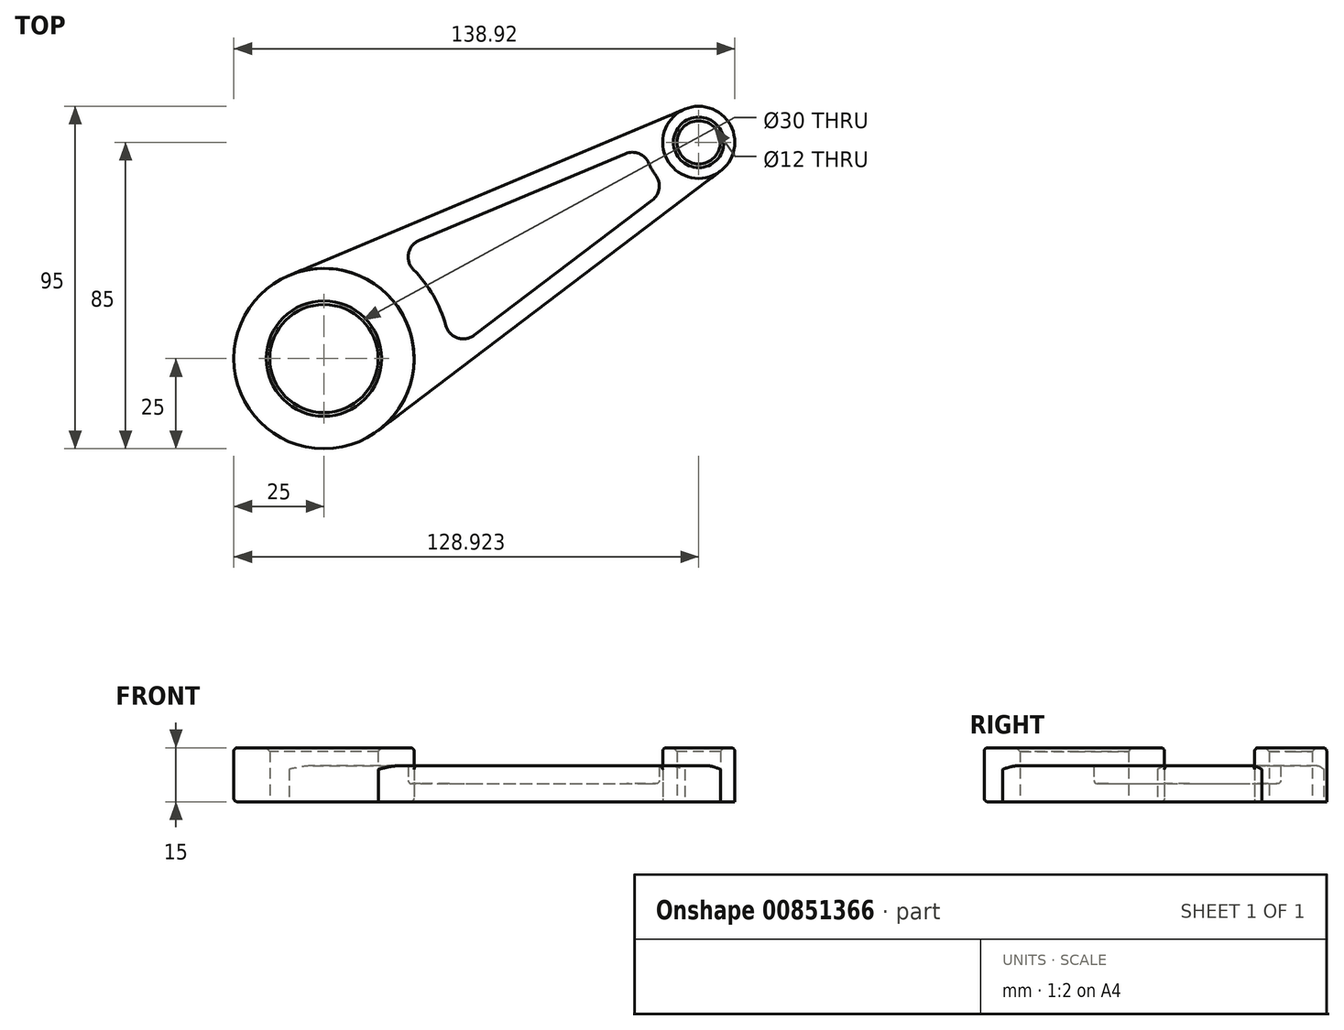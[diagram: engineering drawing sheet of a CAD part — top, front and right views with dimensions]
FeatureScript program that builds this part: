
annotation { "Feature Type Name" : "Feature", "Feature Type Description" : "" }
export const myFeature = defineFeature(function(context is Context, id is Id, definition is map)
    precondition{}
    {
        {
            var Q0;
            Q0=qCreatedBy(makeId("Top.planeOp"),FACE);
            var sketch = newSketch(context, id + "F0", { "sketchPlane" : qUnion([Q0])});
            skLineSegment(sketch, "E0", {"start": v(0, 0) * mm, "end": v(103.92, 60) * mm, "construction": true});
            skLineSegment(sketch, "E1", {"start": v(0, 0) * mm, "end": v(100, 0) * mm, "construction": true});
            skCircle(sketch, "E2", {"center": v(0, 0) * mm, "radius": 25 * mm});
            skCircle(sketch, "E3", {"center": v(103.92, 60) * mm, "radius": 10 * mm});
            skLineSegment(sketch, "E4", {"start": v(-9.7, 23.04) * mm, "end": v(100.04, 69.22) * mm});
            skLineSegment(sketch, "E5", {"start": v(15.1, -19.92) * mm, "end": v(109.97, 52.03) * mm});
            skCircle(sketch, "E6", {"center": v(0, 0) * mm, "radius": 15 * mm});
            skCircle(sketch, "E7", {"center": v(103.92, 60) * mm, "radius": 6 * mm});
            skLineSegment(sketch, "E8.0", {"start": v(34.97, 1.42) * mm, "end": v(95.68, 47.47) * mm});
            skLineSegment(sketch, "E9.0", {"start": v(18.72, 29.57) * mm, "end": v(88.95, 59.12) * mm});
            skArc(sketch, "E10", {"start": v(18.72, 29.57) * mm, "mid": v(30.31, 17.5) * mm, "end": v(34.97, 1.42) * mm});
            skArc(sketch, "E11", {"start": v(88.95, 59.12) * mm, "mid": v(90.93, 52.5) * mm, "end": v(95.68, 47.47) * mm});
            skSolve(sketch);
        }
        {
            var Q0;
            Q0=makeQuery(id+"F0.imprint","IMPRINT",FACE,{"disambiguationData":[TD([[makeQuery(id+"F0.imprint","IMPRINT",EDGE,{"derivedFrom":sQuery(id+"F0.wireOp",EDGE,"E6")}),-1.0]])]});
            var Q1;
            Q1=makeQuery(id+"F0.imprint","IMPRINT",FACE,{"disambiguationData":[TD([[makeQuery(id+"F0.imprint","IMPRINT",EDGE,{"derivedFrom":sQuery(id+"F0.wireOp",EDGE,"E7")}),-1.0]])]});
            extrude(context, id + "F1", {"entities" : qUnion([Q0, Q1]), "depth" : 15 * mm, "offsetDistance" : 25 * mm});
        }
        {
            var Q0;
            {var subQ1=sQuery(id+"F0.wireOp",EDGE,"E4");Q0=makeQuery(id+"F0.imprint","IMPRINT",FACE,{"disambiguationData":[TD([[makeQuery(id+"F0.imprint","IMPRINT",EDGE,{"derivedFrom":subQ1}),-1.0]])]});}
            extrude(context, id + "F2", {"entities" : qUnion([Q0]), "depth" : 10 * mm, "offsetDistance" : 25 * mm});
        }
        {
            var Q0;
            Q0=makeQuery(id+"F0.imprint","IMPRINT",FACE,{"disambiguationData":[TD([[makeQuery(id+"F0.imprint","IMPRINT",EDGE,{"derivedFrom":sQuery(id+"F0.wireOp",EDGE,"E8.0")}),1.0]])]});
            extrude(context, id + "F3", {"entities" : qUnion([Q0]), "operationType" : NewBodyOperationType.ADD, "depth" : 5 * mm, "offsetDistance" : 25 * mm});
        }
        {
            var Q0;
            Q0=makeQuery(id+"F2.opExtrude","CAP_EDGE",EDGE,{"disambiguationData":[OSD([sQuery(id+"F0.wireOp",EDGE,"E2")])],"isStart":false});
            var Q1;
            Q1=makeQuery(id+"F2.opExtrude","CAP_EDGE",EDGE,{"disambiguationData":[OSD([sQuery(id+"F0.wireOp",EDGE,"E3")])],"isStart":false});
            fillet(context, id + "F4", {"entities" : qUnion([Q0, Q1]), "radius" : 1 * mm, "tangentPropagation" : true, "allowEdgeOverflow" : false});
        }
        {
            var Q0;
            Q0=makeQuery(id+"F2.opExtrude","SWEPT_EDGE",EDGE,{"disambiguationData":[OSD([sQuery(id+"F0.wireOp",EDGE,"E9.0"),sQuery(id+"F0.wireOp",EDGE,"E10")])]});
            var Q1;
            Q1=makeQuery(id+"F2.opExtrude","SWEPT_EDGE",EDGE,{"disambiguationData":[OSD([sQuery(id+"F0.wireOp",EDGE,"E8.0"),sQuery(id+"F0.wireOp",EDGE,"E11")])]});
            var Q2;
            Q2=makeQuery(id+"F2.opExtrude","SWEPT_EDGE",EDGE,{"disambiguationData":[OSD([sQuery(id+"F0.wireOp",EDGE,"E9.0"),sQuery(id+"F0.wireOp",EDGE,"E11")])]});
            var Q3;
            Q3=makeQuery(id+"F2.opExtrude","SWEPT_EDGE",EDGE,{"disambiguationData":[OSD([sQuery(id+"F0.wireOp",EDGE,"E8.0"),sQuery(id+"F0.wireOp",EDGE,"E10")])]});
            fillet(context, id + "F5", {"entities" : qUnion([Q0, Q1, Q2, Q3]), "radius" : 5 * mm, "tangentPropagation" : true, "allowEdgeOverflow" : false});
        }
        {
            var Q0;
            Q0=makeQuery(id+"F3.opExtrude","CAP_FACE",FACE,{"disambiguationData":[OSD([sQuery(id+"F0.wireOp",EDGE,"E8.0"),sQuery(id+"F0.wireOp",EDGE,"E9.0"),sQuery(id+"F0.wireOp",EDGE,"E10"),sQuery(id+"F0.wireOp",EDGE,"E11")])],"isStart":false});
            fillet(context, id + "F6", {"entities" : qUnion([Q0]), "radius" : 1 * mm, "tangentPropagation" : true, "allowEdgeOverflow" : false});
        }
        {
            var Q0;
            Q0=makeQuery(id+"F1.opExtrude","CAP_EDGE",EDGE,{"disambiguationData":[OSD([sQuery(id+"F0.wireOp",EDGE,"E3")])],"isStart":false});
            var Q1;
            Q1=makeQuery(id+"F1.opExtrude","CAP_EDGE",EDGE,{"disambiguationData":[OSD([sQuery(id+"F0.wireOp",EDGE,"E2")])],"isStart":false});
            fillet(context, id + "F7", {"entities" : qUnion([Q0, Q1]), "radius" : 1 * mm, "tangentPropagation" : true, "allowEdgeOverflow" : false});
        }
        {
            var Q0;
            Q0=makeQuery(id+"F1.opExtrude","CAP_EDGE",EDGE,{"disambiguationData":[OSD([sQuery(id+"F0.wireOp",EDGE,"E2")])],"isStart":true});
            fillet(context, id + "F8", {"entities" : qUnion([Q0]), "radius" : 1 * mm, "tangentPropagation" : true, "allowEdgeOverflow" : false});
        }
        {
            var Q0;
            Q0=makeQuery(id+"F1.opExtrude","CAP_EDGE",EDGE,{"disambiguationData":[OSD([sQuery(id+"F0.wireOp",EDGE,"E6")])],"isStart":false});
            var Q1;
            Q1=makeQuery(id+"F1.opExtrude","CAP_EDGE",EDGE,{"disambiguationData":[OSD([sQuery(id+"F0.wireOp",EDGE,"E7")])],"isStart":false});
            chamfer(context, id + "F9", {"entities" : qUnion([Q0, Q1]), "width" : 1 * mm, "tangentPropagation" : true});
        }
    });
